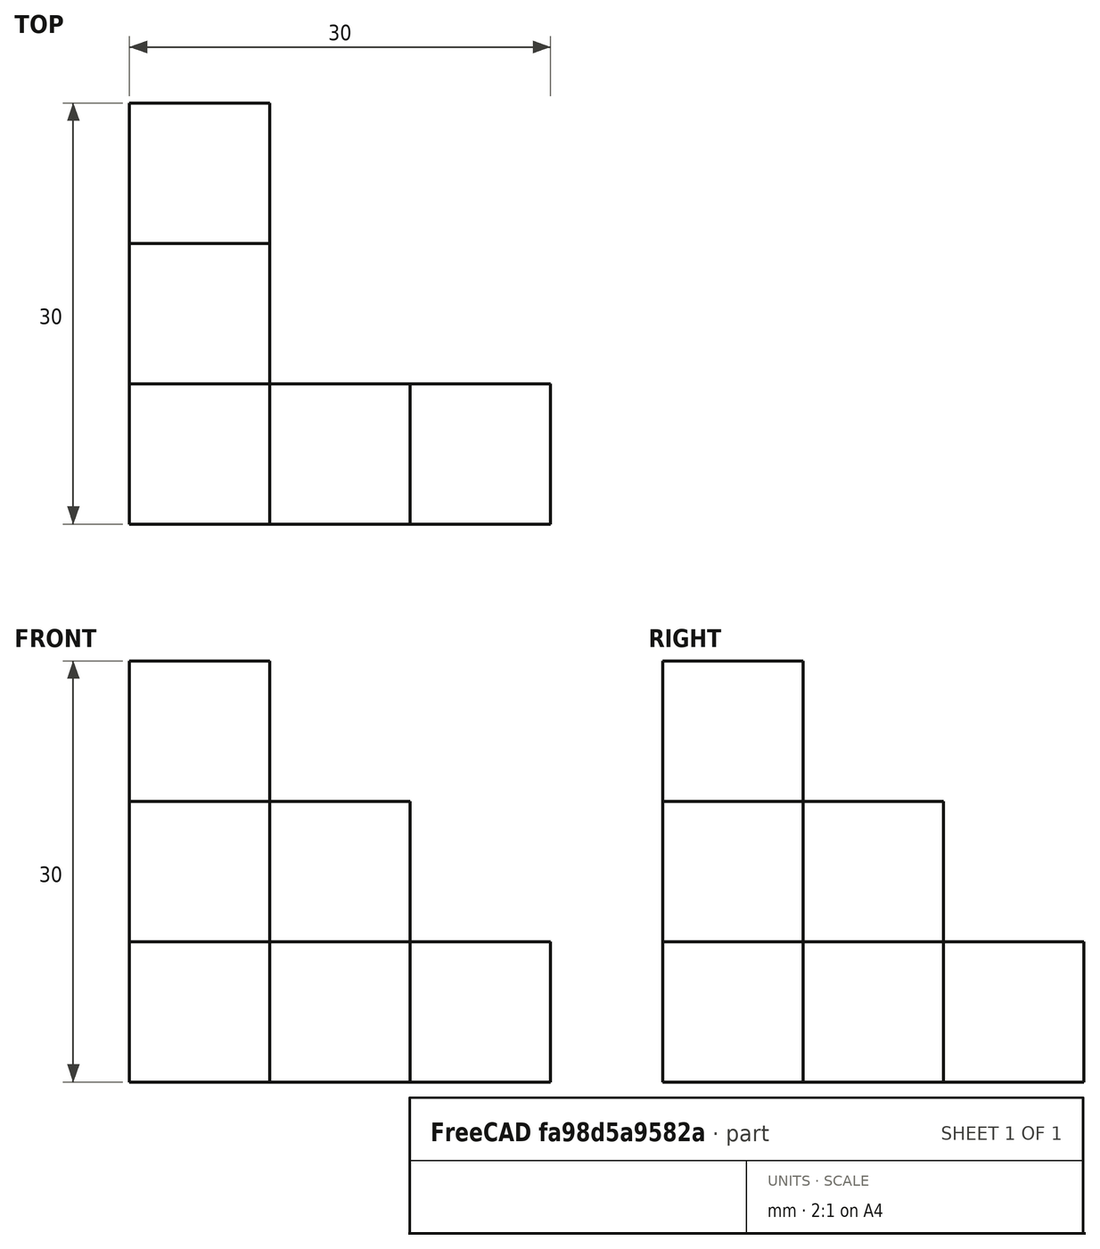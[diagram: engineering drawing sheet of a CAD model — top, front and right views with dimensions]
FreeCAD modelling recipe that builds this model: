
FCSTD DOCUMENT  (FreeCAD 0.21R33771 (Git))
Label: OJT1_T04R01_qbert3nivells_v2
License: All rights reserved
LicenseURL: http://en.wikipedia.org/wiki/All_rights_reserved
objects: Part::Box×9
note: 9 computed .brp shape members not serialized (recipe doc carries the construction recipe); baked Part::Feature solids carry a one-line shape summary decoded from their .brp

FEATURE [Part::Box] Box  label="nivell1_cub1"
  AttacherType = Attacher::AttachEngine3D
  Height = 10
  Length = 10
  Placement = pos=(10,0,0) rot=(0,0,1;0rad)
  Width = 10
FEATURE [Part::Box] Box001  label="nivell1_cub2"
  AttacherType = Attacher::AttachEngine3D
  Height = 10
  Length = 10
  Placement = pos=(20,0,0) rot=(0,0,1;0rad)
  Width = 10
FEATURE [Part::Box] Box002  label="nivell1_cub3"
  AttacherType = Attacher::AttachEngine3D
  Height = 10
  Length = 10
  Width = 10
FEATURE [Part::Box] Box003  label="nivell1_cub4"
  AttacherType = Attacher::AttachEngine3D
  Height = 10
  Length = 10
  Placement = pos=(0,10,0) rot=(0,0,1;0rad)
  Width = 10
FEATURE [Part::Box] Box004  label="nivell1_cub5"
  AttacherType = Attacher::AttachEngine3D
  Height = 10
  Length = 10
  Placement = pos=(0,20,0) rot=(0,0,1;0rad)
  Width = 10
FEATURE [Part::Box] Box005  label="nivell2_cub1"
  AttacherType = Attacher::AttachEngine3D
  Height = 10
  Length = 10
  Placement = pos=(0,0,10) rot=(0,0,1;0rad)
  Width = 10
FEATURE [Part::Box] Box006  label="nivell2_cub2"
  AttacherType = Attacher::AttachEngine3D
  Height = 10
  Length = 10
  Placement = pos=(0,10,10) rot=(0,0,1;0rad)
  Width = 10
FEATURE [Part::Box] Box007  label="nivell2_cub3"
  AttacherType = Attacher::AttachEngine3D
  Height = 10
  Length = 10
  Placement = pos=(10,0,10) rot=(0,0,1;0rad)
  Width = 10
FEATURE [Part::Box] Box008  label="nivell3_cub1"
  AttacherType = Attacher::AttachEngine3D
  Height = 10
  Length = 10
  Placement = pos=(0,0,20) rot=(0,0,1;0rad)
  Width = 10
